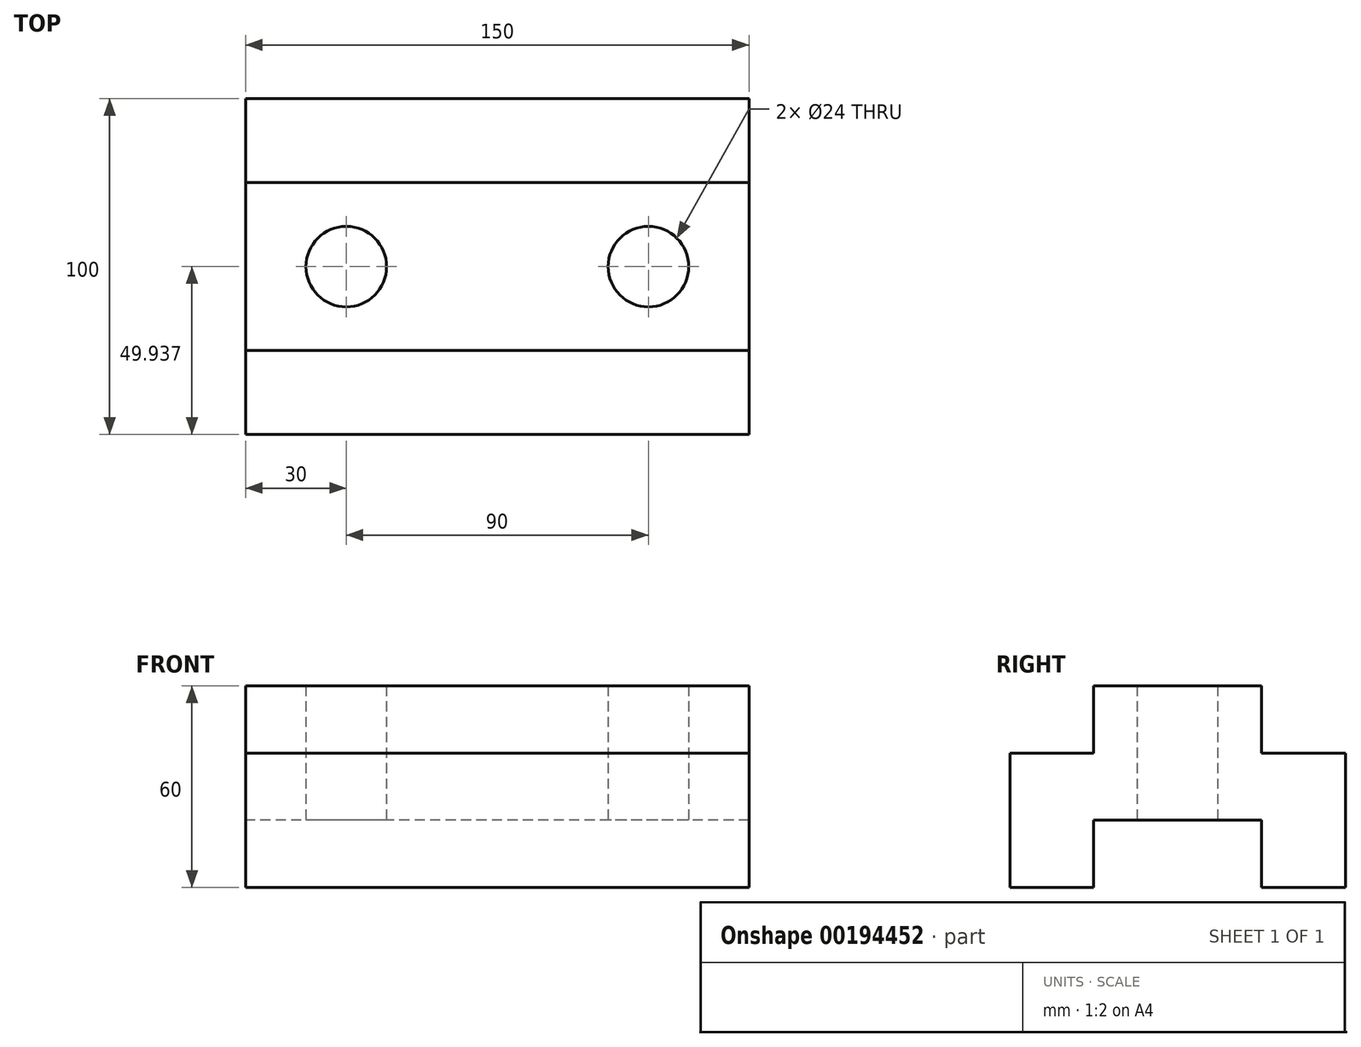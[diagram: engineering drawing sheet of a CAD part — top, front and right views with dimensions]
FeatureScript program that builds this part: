
annotation { "Feature Type Name" : "Feature", "Feature Type Description" : "" }
export const myFeature = defineFeature(function(context is Context, id is Id, definition is map)
    precondition{}
    {
        {
            var Q0;
            Q0=qCreatedBy(makeId("Right.planeOp"),FACE);
            var sketch = newSketch(context, id + "F0", { "sketchPlane" : qUnion([Q0])});
            skLineSegment(sketch, "E0", {"start": v(0, 0) * mm, "end": v(0, 40) * mm});
            skLineSegment(sketch, "E1", {"start": v(0, 40) * mm, "end": v(25, 40) * mm});
            skLineSegment(sketch, "E2", {"start": v(25, 40) * mm, "end": v(25, 60) * mm});
            skLineSegment(sketch, "E3", {"start": v(25, 60) * mm, "end": v(75, 60) * mm});
            skLineSegment(sketch, "E4", {"start": v(75, 60) * mm, "end": v(75, 40) * mm});
            skLineSegment(sketch, "E5", {"start": v(75, 40) * mm, "end": v(100, 40) * mm});
            skLineSegment(sketch, "E6", {"start": v(25, 20) * mm, "end": v(25, 0) * mm});
            skLineSegment(sketch, "E7", {"start": v(25, 0) * mm, "end": v(0, 0) * mm});
            skLineSegment(sketch, "E8", {"start": v(25, 20) * mm, "end": v(75, 20) * mm});
            skLineSegment(sketch, "E9", {"start": v(75, 20) * mm, "end": v(75, 0) * mm});
            skLineSegment(sketch, "E10", {"start": v(75, 0) * mm, "end": v(100, 0) * mm});
            skLineSegment(sketch, "E11", {"start": v(100, 40) * mm, "end": v(100, 0) * mm});
            skSolve(sketch);
        }
        {
            var Q0;
            Q0 = qSketchRegion(id + "F0", true);
            extrude(context, id + "F1", {"entities" : qUnion([Q0]), "depth" : 150 * mm});
        }
        {
            var Q0;
            Q0=qCreatedBy(makeId("Top.planeOp"),FACE);
            var sketch = newSketch(context, id + "F2", { "sketchPlane" : qUnion([Q0])});
            skCircle(sketch, "E12", {"center": v(30, 49.94) * mm, "radius": 12 * mm});
            skCircle(sketch, "E13", {"center": v(120, 49.94) * mm, "radius": 12 * mm});
            skSolve(sketch);
        }
        {
            var Q0;
            Q0 = qSketchRegion(id + "F2", true);
            extrude(context, id + "F3", {"entities" : qUnion([Q0]), "operationType" : NewBodyOperationType.REMOVE, "endBound" : BoundingType.THROUGH_ALL, "depth" : 25 * mm});
        }
    });
